# Revit family: LTUMO
name_source: partatom
category: Mechanical Equipment
units: mm (PartAtom-declared; Revit-internal decimal feet)

## family parameters
Always vertical = Yes
Cut with Voids When Loaded = No
Part Type = Normal
Room Calculation Point = No
Round Connector Dimension = Use Diameter
Shared = No
Work Plane-Based = No

## types (8) — shared parameters
0 = 0"
1" = 1"
1' = 12"
1.5 = 1 1/2"
2" = 2"
2' = 24"
3" = 3"
4" = 4"
Manufacturer = Loren Cook Company
Model = LXULMO
ONE EIGTH = 1/8"
Type Comments = Upblast Exhaust Ventilator Low Pressure X-Stream Propeller Roof Mounted/Belt Drive
URL = www.lorencook.com

## per-type parameters (varying)
| type | (D/2)-2" | (T_SQ/2)+.125" | -D | -D+2" | -D+4" | -T_SQ/4 | A | B | C | C/2 | D | D/2 | RO | RO/2 | T_SQ | T_SQ/2 | T_SQ/4 | WB HEIGHT |
| 20_LTUMO | 11 5/8" | 15 15/16" | -19" | -17" | -15" | -7 29/32" | 44 13/16" | 22" | 25 1/8" | 12 9/16" | 27 1/4" | 13 5/8" | 27 1/8" | 13 9/16" | 31 5/8" | 15 13/16" | 7 29/32" | 18 27/32" |
| 24_LTUMO | 13 5/8" | 17 15/16" | -18" | -16" | -14" | -8 29/32" | 48 13/16" | 22" | 26 3/4" | 13 3/8" | 31 1/4" | 15 5/8" | 31 1/8" | 15 9/16" | 35 5/8" | 17 13/16" | 8 29/32" | 20 1/16" |
| 30_LTUMO | 16 5/8" | 20 15/16" | -18" | -16" | -14" | -10 13/32" | 54 13/16" | 22" | 33 3/4" | 16 7/8" | 37 1/4" | 18 5/8" | 37 1/8" | 18 9/16" | 41 5/8" | 20 13/16" | 10 13/32" | 25 5/16" |
| 36_LTUMO | 19 5/8" | 23 15/16" | -18" | -16" | -14" | -11 29/32" | 64 13/16" | 24" | 38" | 19" | 43 1/4" | 21 5/8" | 43 1/8" | 21 9/16" | 47 5/8" | 23 13/16" | 11 29/32" | 28 1/2" |
| 42_LTUMO | 22 5/8" | 26 15/16" | -18" | -16" | -14" | -13 13/32" | 70 11/16" | 24" | 46 3/8" | 23 3/16" | 49 1/4" | 24 5/8" | 49 1/8" | 24 9/16" | 53 5/8" | 26 13/16" | 13 13/32" | 34 25/32" |
| 48_LTUMO | 25 5/8" | 29 15/16" | -21" | -19" | -17" | -14 29/32" | 76 11/16" | 24" | 49 5/8" | 24 13/16" | 55 1/4" | 27 5/8" | 55 1/8" | 27 9/16" | 59 5/8" | 29 13/16" | 14 29/32" | 37 7/32" |
| 54_LTUMO | 28 5/8" | 32 15/16" | -25" | -23" | -21" | -16 13/32" | 83 11/16" | 28" | 48" | 24" | 61 1/4" | 30 5/8" | 61 1/8" | 30 9/16" | 65 5/8" | 32 13/16" | 16 13/32" | 36" |
| 60_LTUMO | 31 5/8" | 35 15/16" | -25" | -23" | -21" | -17 29/32" | 93 11/16" | 32" | 50 3/4" | 25 3/8" | 67 1/4" | 33 5/8" | 67 1/8" | 33 9/16" | 71 5/8" | 35 13/16" | 17 29/32" | 38 1/16" |

## geometry (parser evidence)
native form markers: Sweep x2
no freeform markers — native parametric forms only
